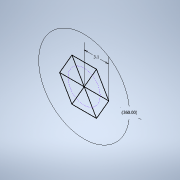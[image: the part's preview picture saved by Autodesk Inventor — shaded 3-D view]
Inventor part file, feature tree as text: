
AUTODESK INVENTOR PART (.ipt)
format: ipt  version: 2022 (Build 260153000, 153)  size: 103,424 bytes
history: native  units: mm
features: extrude x1, sketch x1
ambient origin geometry x8: Origin, YZ Plane, XZ Plane, XY Plane, X Axis, Y Axis, Z Axis, Center Point
bodies: Solid1 (feature_tree)
feature tree (2):
  extrude  "Extrusion1"  Depth=40.0mm TaperAngle=360.0deg
  sketch  "Sketch1"  dims[d0=3.1mm d1=60.0mm d3=360.0deg d5=40.0mm d6=0.0mm]
